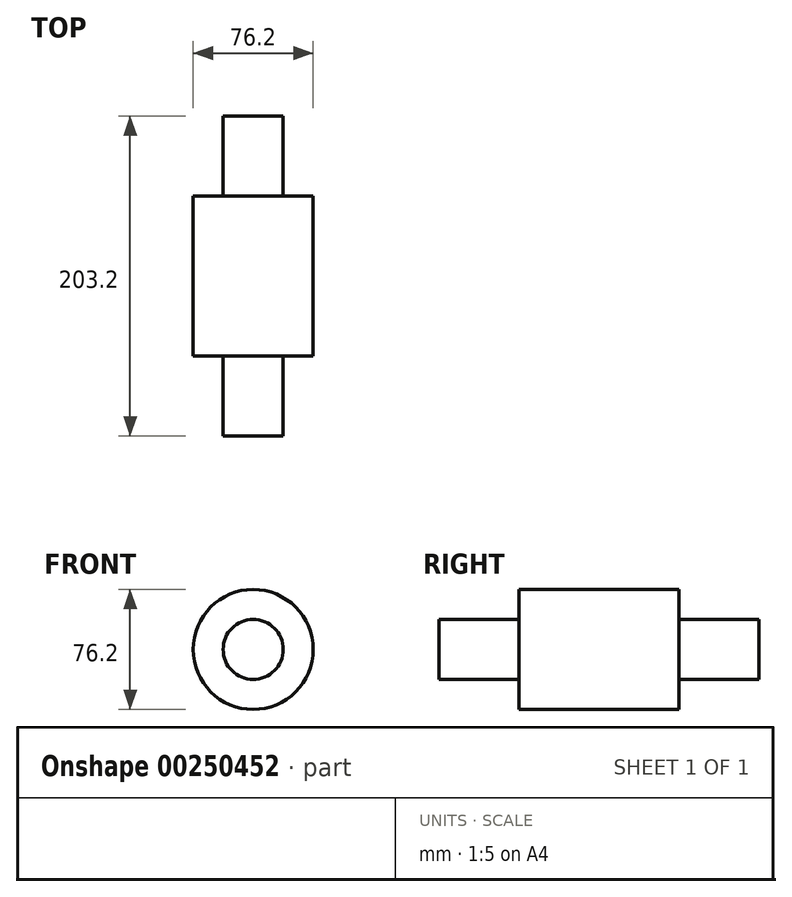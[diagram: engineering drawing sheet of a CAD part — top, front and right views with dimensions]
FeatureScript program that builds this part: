
annotation { "Feature Type Name" : "Feature", "Feature Type Description" : "" }
export const myFeature = defineFeature(function(context is Context, id is Id, definition is map)
    precondition{}
    {
        {
            var Q0;
            Q0=qCreatedBy(makeId("Front.planeOp"),FACE);
            var sketch = newSketch(context, id + "F0", { "sketchPlane" : qUnion([Q0])});
            skCircle(sketch, "E0", {"center": v(0, 0) * mm, "radius": 38.1 * mm});
            skCircle(sketch, "E1", {"center": v(0, 0) * mm, "radius": 19.05 * mm});
            skSolve(sketch);
        }
        {
            var Q0;
            Q0=makeQuery(id+"F0.imprint","IMPRINT",FACE,{"disambiguationData":[TD([[makeQuery(id+"F0.imprint","IMPRINT",EDGE,{"derivedFrom":sQuery(id+"F0.wireOp",EDGE,"E0")}),1.0]])]});
            var Q1;
            Q1=sQuery(id+"F0.wireOp",EDGE,"E0");
            var Q2;
            Q2=sQuery(id+"F0.wireOp",EDGE,"E1");
            extrude(context, id + "F1", {"entities" : qUnion([Q0]), "surfaceEntities" : qUnion([Q1, Q2]), "endBound" : BoundingType.SYMMETRIC, "depth" : 101.6 * mm});
        }
        {
            var Q0;
            Q0=makeQuery(id+"F0.imprint","IMPRINT",FACE,{"disambiguationData":[TD([[makeQuery(id+"F0.imprint","IMPRINT",EDGE,{"derivedFrom":sQuery(id+"F0.wireOp",EDGE,"E1")}),1.0]])]});
            extrude(context, id + "F2", {"entities" : qUnion([Q0]), "operationType" : NewBodyOperationType.ADD, "endBound" : BoundingType.SYMMETRIC, "depth" : 203.2 * mm});
        }
    });
